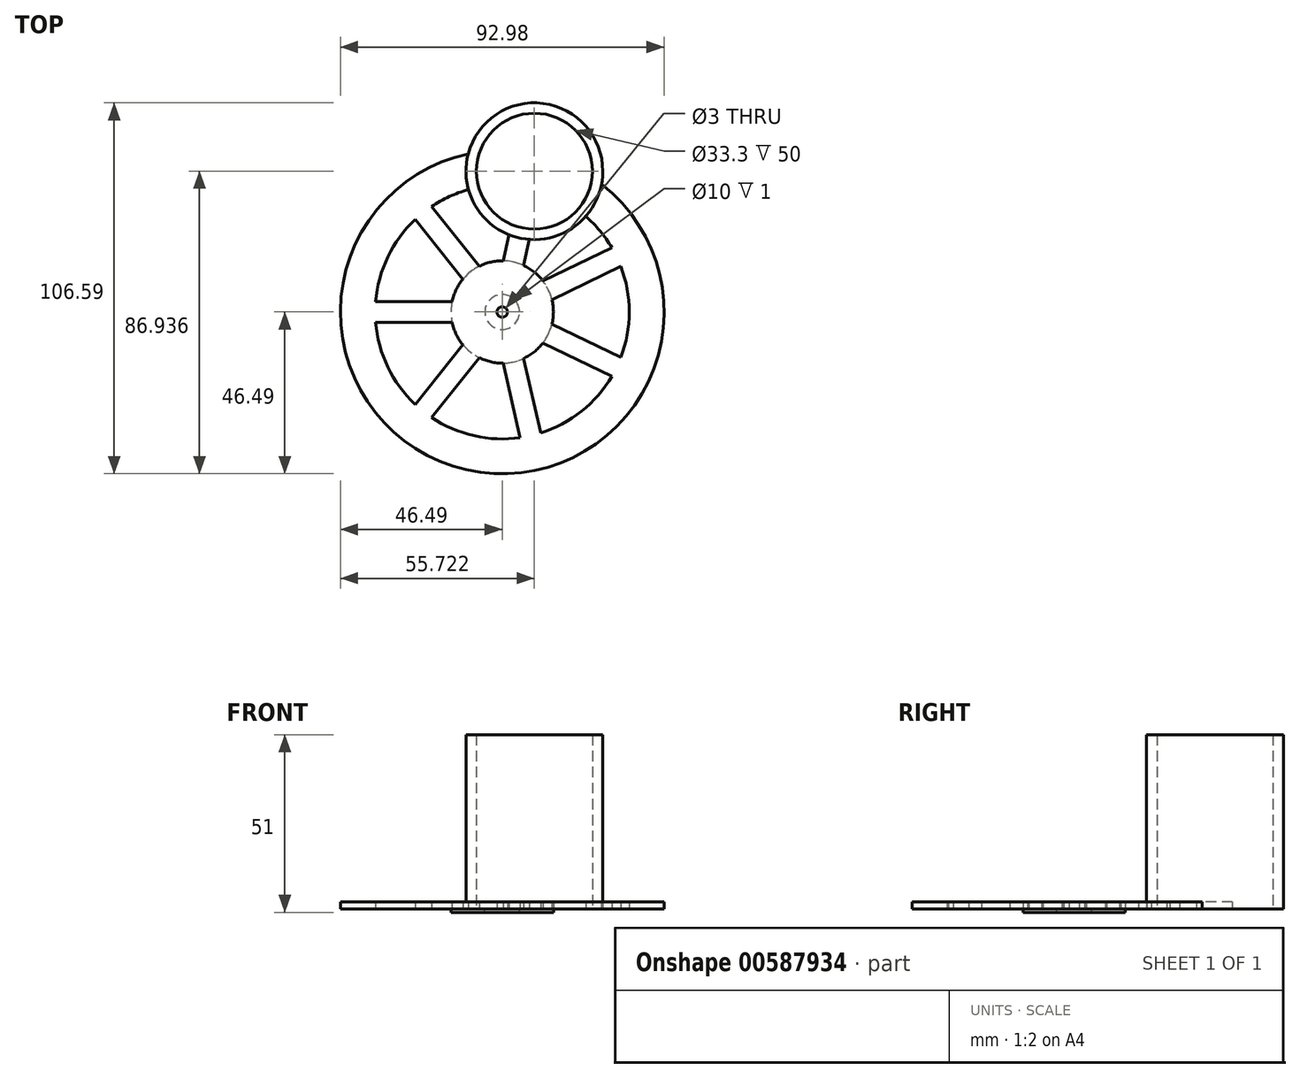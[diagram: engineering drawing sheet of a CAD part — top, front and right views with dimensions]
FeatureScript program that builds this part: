
annotation { "Feature Type Name" : "Feature", "Feature Type Description" : "" }
export const myFeature = defineFeature(function(context is Context, id is Id, definition is map)
    precondition{}
    {
        {
            var Q0;
            Q0=qCreatedBy(makeId("Top.planeOp"),FACE);
            var sketch = newSketch(context, id + "F0", { "sketchPlane" : qUnion([Q0])});
            skCircle(sketch, "E0", {"center": v(-41.49, 0) * mm, "radius": 16.65 * mm, "construction": true});
            skCircle(sketch, "E1.cCircle", {"center": v(0, 0) * mm, "radius": 41.49 * mm, "construction": true});
            skLineSegment(sketch, "E1.0", {"start": v(-41.49, 0) * mm, "end": v(-25.87, 32.43) * mm, "construction": true});
            skLineSegment(sketch, "E1.1", {"start": v(-25.87, 32.43) * mm, "end": v(9.23, 40.45) * mm, "construction": true});
            skLineSegment(sketch, "E1.2", {"start": v(9.23, 40.45) * mm, "end": v(37.38, 18) * mm, "construction": true});
            skLineSegment(sketch, "E1.3", {"start": v(37.38, 18) * mm, "end": v(37.38, -18) * mm, "construction": true});
            skLineSegment(sketch, "E1.4", {"start": v(37.38, -18) * mm, "end": v(9.23, -40.45) * mm, "construction": true});
            skLineSegment(sketch, "E1.5", {"start": v(9.23, -40.45) * mm, "end": v(-25.87, -32.43) * mm, "construction": true});
            skLineSegment(sketch, "E1.6", {"start": v(-25.87, -32.43) * mm, "end": v(-41.49, 0) * mm, "construction": true});
            skCircle(sketch, "E2", {"center": v(-25.87, 32.43) * mm, "radius": 16.65 * mm, "construction": true});
            skCircle(sketch, "E3", {"center": v(9.23, 40.45) * mm, "radius": 16.65 * mm});
            skCircle(sketch, "E4", {"center": v(37.38, 18) * mm, "radius": 16.65 * mm, "construction": true});
            skCircle(sketch, "E5", {"center": v(37.38, -18) * mm, "radius": 16.65 * mm, "construction": true});
            skCircle(sketch, "E6", {"center": v(9.23, -40.45) * mm, "radius": 16.65 * mm, "construction": true});
            skCircle(sketch, "E7", {"center": v(-25.87, -32.43) * mm, "radius": 16.65 * mm, "construction": true});
            skCircle(sketch, "E8", {"center": v(0, 0) * mm, "radius": 62.5 * mm, "construction": true});
            skCircle(sketch, "E9", {"center": v(0, 0) * mm, "radius": 55 * mm, "construction": true});
            skCircle(sketch, "E10", {"center": v(0, 0) * mm, "radius": 15 * mm, "construction": true});
            skCircle(sketch, "E11.0", {"center": v(0, 0) * mm, "radius": 14.7 * mm});
            skCircle(sketch, "E12", {"center": v(0, 0) * mm, "radius": 10 * mm, "construction": true});
            skCircle(sketch, "E13", {"center": v(0, 0) * mm, "radius": 5.15 * mm, "construction": true});
            skCircle(sketch, "E14.0", {"center": v(0, 0) * mm, "radius": 46.49 * mm});
            skCircle(sketch, "E15.0", {"center": v(0, 0) * mm, "radius": 36.49 * mm});
            skCircle(sketch, "E16", {"center": v(0, 0) * mm, "radius": 5 * mm});
            skCircle(sketch, "E17.0", {"center": v(9.23, 40.45) * mm, "radius": 19.65 * mm});
            skLineSegment(sketch, "E18", {"start": v(-36.36, 3) * mm, "end": v(-14.4, 3) * mm});
            skLineSegment(sketch, "E19.MirrorCS", {"start": v(-36.36, -3) * mm, "end": v(-14.4, -3) * mm});
            skCircle(sketch, "E20", {"center": v(0, 0) * mm, "radius": 1.5 * mm});
            skSolve(sketch);
        }
        {
            var Q0;
            {var subQ2=sQuery(id+"F0.wireOp",EDGE,"E17.0");var subQ6=sQuery(id+"F0.wireOp",EDGE,"E14.0");var subQ7=makeQuery(id+"F0.imprint","INTERSECT",VERTEX,{"disambiguationData":[OD(0.0)],"derivedFrom":[subQ6,subQ2]});Q0=makeQuery(id+"F0.imprint","IMPRINT",FACE,{"disambiguationData":[TD([[makeQuery(id+"F0.imprint","IMPRINT",EDGE,{"disambiguationData":[TD([[subQ7,1.0]])],"derivedFrom":subQ6}),1.0]])]});}
            var Q1;
            Q1=makeQuery(id+"F0.imprint","IMPRINT",FACE,{"disambiguationData":[TD([[makeQuery(id+"F0.imprint","IMPRINT",EDGE,{"derivedFrom":sQuery(id+"F0.wireOp",EDGE,"E16")}),-1.0]])]});
            var Q2;
            Q2=makeQuery(id+"F0.imprint","IMPRINT",FACE,{"disambiguationData":[TD([[makeQuery(id+"F0.imprint","IMPRINT",EDGE,{"derivedFrom":sQuery(id+"F0.wireOp",EDGE,"E16")}),1.0]])]});
            extrude(context, id + "F1", {"entities" : qUnion([Q0, Q1, Q2]), "depth" : 2 * mm, "offsetDistance" : 25 * mm});
        }
        {
            var Q0;
            {var subQ0=sQuery(id+"F0.wireOp",EDGE,"E18");Q0=makeQuery(id+"F0.imprint","IMPRINT",FACE,{"disambiguationData":[TD([[makeQuery(id+"F0.imprint","IMPRINT",EDGE,{"derivedFrom":subQ0}),-1.0]])]});}
            extrude(context, id + "F2", {"entities" : qUnion([Q0]), "depth" : 2 * mm, "offsetDistance" : 25 * mm});
        }
        {
            var Q0;
            Q0=makeQuery(id+"F2.opExtrude","SWEPT_BODY",BODY,{"disambiguationData":[OSD([sQuery(id+"F0.wireOp",EDGE,"E11.0"),sQuery(id+"F0.wireOp",EDGE,"E15.0"),sQuery(id+"F0.wireOp",EDGE,"E18"),sQuery(id+"F0.wireOp",EDGE,"E19.MirrorCS")])]});
            var Q1;
            Q1=makeQuery(id+"F1.opExtrude","CAP_EDGE",EDGE,{"disambiguationData":[OSD([sQuery(id+"F0.wireOp",EDGE,"E11.0")])],"isStart":false});
            circularPattern(context, id + "F3", {"operationType" : NewBodyOperationType.ADD, "entities" : qUnion([Q0]), "axis" : qUnion([Q1]), "angle" : 360 * degree, "instanceCount" : 7, "equalSpace" : true});
        }
        {
            var Q0;
            {var subQ0=sQuery(id+"F0.wireOp",EDGE,"E15.0");var subQ1=sQuery(id+"F0.wireOp",EDGE,"E3");var subQ2=makeQuery(id+"F0.imprint","INTERSECT",VERTEX,{"disambiguationData":[OD(0.0)],"derivedFrom":[subQ1,subQ0]});Q0=makeQuery(id+"F0.imprint","IMPRINT",FACE,{"disambiguationData":[TD([[makeQuery(id+"F0.imprint","IMPRINT",EDGE,{"disambiguationData":[TD([[subQ2,-1.0]])],"derivedFrom":subQ1}),1.0]])]});}
            extrude(context, id + "F4", {"entities" : qUnion([Q0]), "operationType" : NewBodyOperationType.REMOVE, "depth" : 25 * mm, "offsetDistance" : 25 * mm});
        }
        {
            var Q0;
            {var subQ0=sQuery(id+"F0.wireOp",EDGE,"E14.0");var subQ1=sQuery(id+"F0.wireOp",EDGE,"E3");var subQ2=makeQuery(id+"F0.imprint","INTERSECT",VERTEX,{"disambiguationData":[OD(0.0)],"derivedFrom":[subQ1,subQ0]});Q0=makeQuery(id+"F0.imprint","IMPRINT",FACE,{"disambiguationData":[TD([[makeQuery(id+"F0.imprint","IMPRINT",EDGE,{"disambiguationData":[TD([[subQ2,1.0]])],"derivedFrom":subQ1}),-1.0]])]});}
            var Q1;
            {var subQ0=sQuery(id+"F0.wireOp",EDGE,"E15.0");var subQ1=sQuery(id+"F0.wireOp",EDGE,"E3");var subQ2=makeQuery(id+"F0.imprint","INTERSECT",VERTEX,{"disambiguationData":[OD(0.0)],"derivedFrom":[subQ1,subQ0]});Q1=makeQuery(id+"F0.imprint","IMPRINT",FACE,{"disambiguationData":[TD([[makeQuery(id+"F0.imprint","IMPRINT",EDGE,{"disambiguationData":[TD([[subQ2,1.0]])],"derivedFrom":subQ1}),-1.0]])]});}
            var Q2;
            {var subQ0=sQuery(id+"F0.wireOp",EDGE,"E15.0");var subQ1=sQuery(id+"F0.wireOp",EDGE,"E3");var subQ2=makeQuery(id+"F0.imprint","INTERSECT",VERTEX,{"disambiguationData":[OD(1.0)],"derivedFrom":[subQ1,subQ0]});Q2=makeQuery(id+"F0.imprint","IMPRINT",FACE,{"disambiguationData":[TD([[makeQuery(id+"F0.imprint","IMPRINT",EDGE,{"disambiguationData":[TD([[subQ2,-1.0]])],"derivedFrom":subQ1}),-1.0]])]});}
            var Q3;
            {var subQ0=sQuery(id+"F0.wireOp",EDGE,"E15.0");var subQ1=sQuery(id+"F0.wireOp",EDGE,"E3");var subQ2=makeQuery(id+"F0.imprint","INTERSECT",VERTEX,{"disambiguationData":[OD(0.0)],"derivedFrom":[subQ1,subQ0]});Q3=makeQuery(id+"F0.imprint","IMPRINT",FACE,{"disambiguationData":[TD([[makeQuery(id+"F0.imprint","IMPRINT",EDGE,{"disambiguationData":[TD([[subQ2,-1.0]])],"derivedFrom":subQ1}),-1.0]])]});}
            extrude(context, id + "F5", {"entities" : qUnion([Q0, Q1, Q2, Q3]), "operationType" : NewBodyOperationType.ADD, "depth" : 50 * mm, "offsetDistance" : 25 * mm});
        }
        {
            var Q0;
            Q0=makeQuery(id+"F0.imprint","IMPRINT",FACE,{"disambiguationData":[TD([[makeQuery(id+"F0.imprint","IMPRINT",EDGE,{"derivedFrom":sQuery(id+"F0.wireOp",EDGE,"E16")}),-1.0]])]});
            extrude(context, id + "F6", {"entities" : qUnion([Q0]), "operationType" : NewBodyOperationType.ADD, "oppositeDirection" : true, "depth" : 1 * mm, "offsetDistance" : 25 * mm});
        }
    });
